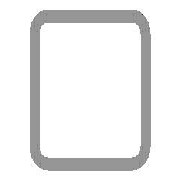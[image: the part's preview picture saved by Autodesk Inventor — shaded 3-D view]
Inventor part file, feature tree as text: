
AUTODESK INVENTOR PART (.ipt)
format: ipt  version: 2022.1 (Build 261234000, 234)  size: 135,168 bytes
history: native  units: mm (DEFAULTED — no unit token found)
features: other x4, sketch x3, plane x1
ambient origin geometry x8: Origin, YZ Plane, XZ Plane, XY Plane, X Axis, Y Axis, Z Axis, Center Point
bodies: Solid1 (feature_tree), Body (feature_tree)
feature tree (8):
  parser-record x1  (decoder bookkeeping rows leaked as tree rows — omitted from the tree; the rows remain in map.json)
  other  "Driven Length"
  other  "Start Plane"
  other  "End Plane"
  sketch  "Sketch"  dims[d7=7.5mm d10=40.0mm d11=40.0mm d12=5.0mm d13=-0.0mm d14=480.0mm d15=20.0mm d16=20.0mm d17=90.0deg d18=480.0mm]
  sketch  "Sketch3"  dims[d3=480.0mm]
  plane  "Work Plane3"
  sketch  "Sketch4"  dims[d4=0.0mm]
